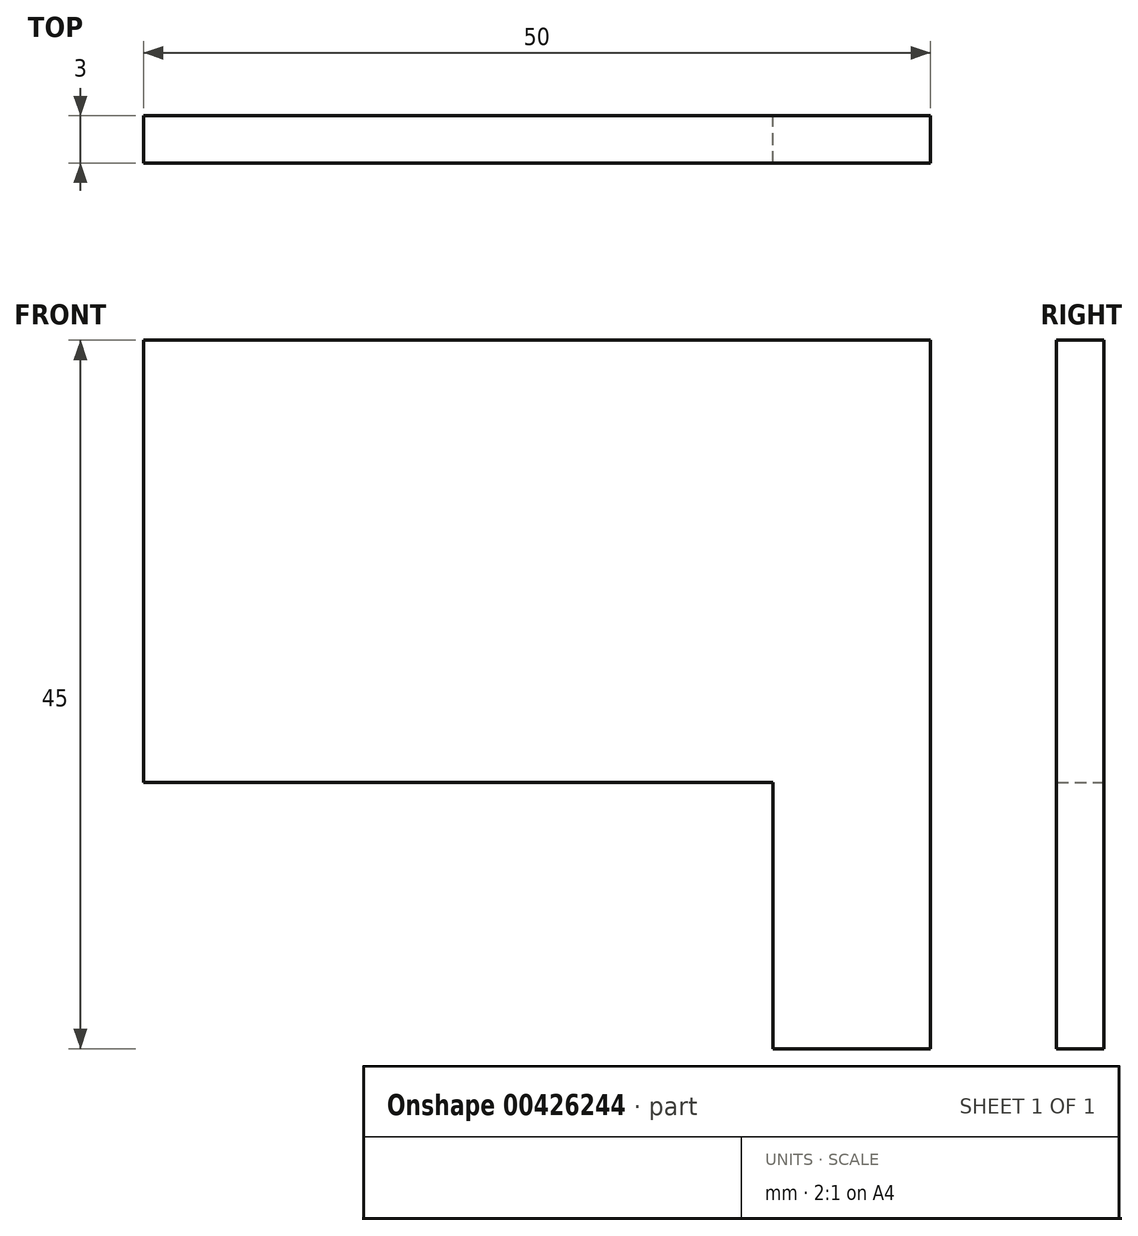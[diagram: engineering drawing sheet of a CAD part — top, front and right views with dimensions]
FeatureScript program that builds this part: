
annotation { "Feature Type Name" : "Feature", "Feature Type Description" : "" }
export const myFeature = defineFeature(function(context is Context, id is Id, definition is map)
    precondition{}
    {
        {
            var Q0;
            Q0=qCreatedBy(makeId("Front.planeOp"),FACE);
            var sketch = newSketch(context, id + "F0", { "sketchPlane" : qUnion([Q0])});
            skLineSegment(sketch, "E0.bottom", {"start": v(25, -22.5) * mm, "end": v(15, -22.5) * mm});
            skLineSegment(sketch, "E0.top", {"start": v(25, 22.5) * mm, "end": v(-25, 22.5) * mm});
            skLineSegment(sketch, "E0.left", {"start": v(25, -22.5) * mm, "end": v(25, 22.5) * mm});
            skLineSegment(sketch, "E0.right", {"start": v(-25, -5.6) * mm, "end": v(-25, 22.5) * mm});
            skPoint(sketch, "E0.middle", {"position": v(0, 0) * mm});
            skLineSegment(sketch, "E1", {"start": v(-25, -5.6) * mm, "end": v(15, -5.6) * mm});
            skLineSegment(sketch, "E2", {"start": v(15, -5.6) * mm, "end": v(15, -22.5) * mm});
            skPoint(sketch, "E3.orphan", {"position": v(-25, -22.5) * mm});
            skSolve(sketch);
        }
        {
            var Q0;
            Q0 = qSketchRegion(id + "F0", true);
            extrude(context, id + "F1", {"entities" : qUnion([Q0]), "depth" : 3 * mm});
        }
    });
